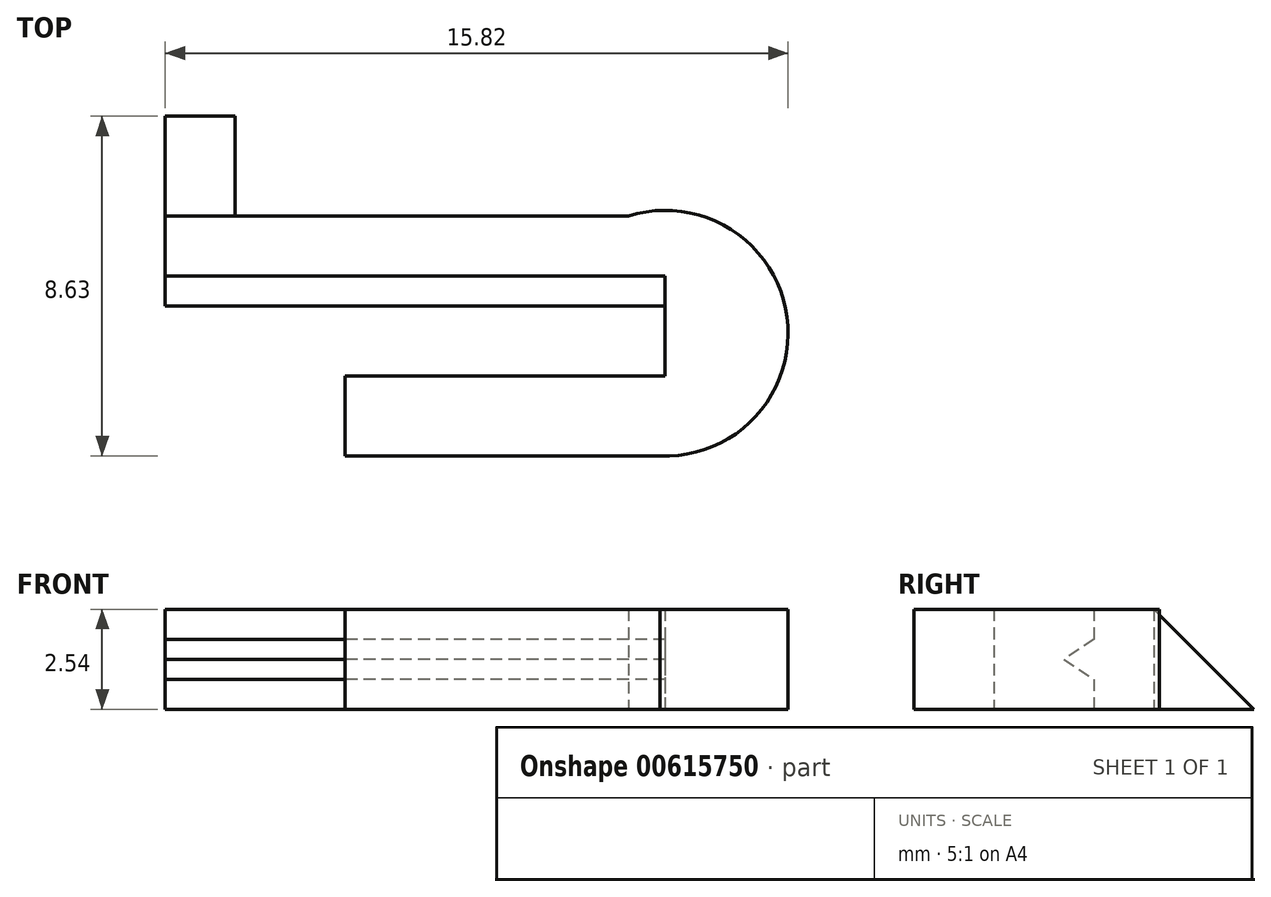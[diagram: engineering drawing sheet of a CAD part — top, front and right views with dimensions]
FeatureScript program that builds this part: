
annotation { "Feature Type Name" : "Feature", "Feature Type Description" : "" }
export const myFeature = defineFeature(function(context is Context, id is Id, definition is map)
    precondition{}
    {
        {
            var Q0;
            Q0=qCreatedBy(makeId("Top.planeOp"),FACE);
            var sketch = newSketch(context, id + "F0", { "sketchPlane" : qUnion([Q0])});
            skLineSegment(sketch, "E0", {"start": v(0, 0) * mm, "end": v(12.7, 0) * mm});
            skLineSegment(sketch, "E1", {"start": v(12.7, 0) * mm, "end": v(12.7, -2.54) * mm});
            skLineSegment(sketch, "E2", {"start": v(12.7, -2.54) * mm, "end": v(4.57, -2.54) * mm});
            skLineSegment(sketch, "E3", {"start": v(4.57, -2.54) * mm, "end": v(4.57, -4.57) * mm});
            skLineSegment(sketch, "E4", {"start": v(4.57, -4.57) * mm, "end": v(12.57, -4.57) * mm});
            skLineSegment(sketch, "E5", {"start": v(0, 0) * mm, "end": v(0, 1.52) * mm});
            skLineSegment(sketch, "E6", {"start": v(0, 1.52) * mm, "end": v(11.76, 1.52) * mm});
            skArc(sketch, "E7", {"start": v(12.57, -4.57) * mm, "mid": v(15.8, -1.04) * mm, "end": v(11.76, 1.52) * mm});
            skSolve(sketch);
        }
        {
            var Q0;
            Q0=qSketchRegion(id+"F0",true);
            extrude(context, id + "F1", {"entities" : qUnion([Q0]), "endBound" : BoundingType.SYMMETRIC, "depth" : 2.54 * mm, "offsetDistance" : 25.4 * mm});
        }
        {
            var Q0;
            Q0=makeQuery(id+"F1.opExtrude","SWEPT_FACE",FACE,{"disambiguationData":[OSD([sQuery(id+"F0.wireOp",EDGE,"E5")])]});
            var sketch = newSketch(context, id + "F2", { "sketchPlane" : qUnion([Q0])});
            skLineSegment(sketch, "E8", {"start": v(0, 0.5) * mm, "end": v(0.76, 0) * mm});
            skLineSegment(sketch, "E9", {"start": v(0.76, 0) * mm, "end": v(0, -0.5) * mm});
            skLineSegment(sketch, "E10", {"start": v(0, -0.5) * mm, "end": v(0, 0.5) * mm});
            skSolve(sketch);
        }
        {
            var Q0;
            Q0=qSketchRegion(id+"F2",true);
            extrude(context, id + "F3", {"entities" : qUnion([Q0]), "operationType" : NewBodyOperationType.ADD, "endBound" : BoundingType.UP_TO_NEXT, "oppositeDirection" : true, "depth" : 25.4 * mm, "offsetDistance" : 25.4 * mm});
        }
        {
            var Q0;
            Q0=makeQuery(id+"F6.boolean.opBoolean","MERGE",FACE,{"derivedFrom":[makeQuery(id+"F3.boolean.opBoolean","MERGE",FACE,{"derivedFrom":[makeQuery(id+"F1.opExtrude","SWEPT_FACE",FACE,{"disambiguationData":[OSD([sQuery(id+"F0.wireOp",EDGE,"E5")])]}),makeQuery(id+"F3.opExtrude","CAP_FACE",FACE,{"disambiguationData":[OSD([sQuery(id+"F2.wireOp",EDGE,"E8"),sQuery(id+"F2.wireOp",EDGE,"E9"),sQuery(id+"F2.wireOp",EDGE,"E10")])],"isStart":true})]}),makeQuery(id+"F6.opExtrude","CAP_FACE",FACE,{"disambiguationData":[OSD([sQuery(id+"F5.wireOp",EDGE,"E11"),sQuery(id+"F5.wireOp",EDGE,"E12"),sQuery(id+"F5.wireOp",EDGE,"E13")])],"isStart":true})]});
            cPlane(context, id + "F4", {"entities" : qUnion([Q0]), "cplaneType" : CPlaneType.OFFSET, "offset" : 0 * mm, "oppositeDirection" : true, "width" : 152.4 * mm, "height" : 152.4 * mm});
        }
        {
            var Q0;
            Q0=qCreatedBy(id+"F4.planeOp",FACE);
            var sketch = newSketch(context, id + "F5", { "sketchPlane" : qUnion([Q0])});
            skLineSegment(sketch, "E11", {"start": v(-1.52, -1.27) * mm, "end": v(-4.06, -1.27) * mm});
            skLineSegment(sketch, "E12", {"start": v(-4.06, -1.27) * mm, "end": v(-1.52, 1.27) * mm});
            skLineSegment(sketch, "E13", {"start": v(-1.52, 1.27) * mm, "end": v(-1.52, -1.27) * mm});
            skSolve(sketch);
        }
        {
            var Q0;
            Q0=qSketchRegion(id+"F5",true);
            extrude(context, id + "F6", {"entities" : qUnion([Q0]), "operationType" : NewBodyOperationType.ADD, "oppositeDirection" : true, "depth" : 1.78 * mm, "offsetDistance" : 25.4 * mm});
        }
        {
            var Q0;
            Q0=makeQuery(id+"F1.opExtrude","SWEPT_BODY",BODY,{"disambiguationData":[OSD([sQuery(id+"F0.wireOp",EDGE,"E0"),sQuery(id+"F0.wireOp",EDGE,"E1"),sQuery(id+"F0.wireOp",EDGE,"E2"),sQuery(id+"F0.wireOp",EDGE,"E3"),sQuery(id+"F0.wireOp",EDGE,"E4"),sQuery(id+"F0.wireOp",EDGE,"E5"),sQuery(id+"F0.wireOp",EDGE,"E6"),sQuery(id+"F0.wireOp",EDGE,"E7")])]});
            transform(context, id + "F7", {"entities" : qUnion([Q0]), "transformType" : TransformType.TRANSLATION_3D, "dx" : 0 * mm, "dy" : 0 * mm, "dz" : 0 * mm, "makeCopy" : true});
        }
        {
            var Q0;
            Q0=makeQuery(id+"F7.opPattern","COPY",BODY,{"derivedFrom":makeQuery(id+"F1.opExtrude","SWEPT_BODY",BODY,{"disambiguationData":[OSD([sQuery(id+"F0.wireOp",EDGE,"E0"),sQuery(id+"F0.wireOp",EDGE,"E1"),sQuery(id+"F0.wireOp",EDGE,"E2"),sQuery(id+"F0.wireOp",EDGE,"E3"),sQuery(id+"F0.wireOp",EDGE,"E4"),sQuery(id+"F0.wireOp",EDGE,"E5"),sQuery(id+"F0.wireOp",EDGE,"E6"),sQuery(id+"F0.wireOp",EDGE,"E7")])]}),"instanceName":"1"});
            deleteBodies(context, id + "F8", {"entities" : qUnion([Q0])});
        }
    });
